AUTODESK INVENTOR PART (.ipt)
format: ipt  version: 2016 (Build 200138000, 138)  size: 852,480 bytes
history: native  units: mm
features: other x69, extrude x8, helix x3, sketch x3, sweep x2, plane x1
ambient origin geometry x8: Origin, YZ Plane, XZ Plane, XY Plane, X Axis, Y Axis, Z Axis, Center Point
bodies: Solid1 (feature_tree)
feature tree (86):
  other  "主线圈路径 (右)"
  other  "剖切工作平面 (右)"
  other  "起始工作平面 (右)"
  other  "结束工作平面 (右)"
  other  "结束切割工作平面 (右)"
  other  "起始切割工作平面 (右)"
  other  "平端切割工作平面 1 (右)"
  other  "平端切割工作平面 2 (右)"
  sweep  "Main Coil Feature(R)"
  other  "起始过渡线圈 1 (右)"
  helix  "Coil  Start Transition 2(R)"  [1 undecoded]
  helix  "Coil  Start Transition 3(R)"  [1 undecoded]
  helix  "Coil  Start Transition 4(R)"  [1 undecoded]
  other  "起始端线圈 (右)"
  extrude  "起始切割特征 (右)"  Depth=10.0mm
  other  "结束过渡线圈 1 (右)"
  other  "结束过渡线圈 2 (右)"
  other  "结束过渡线圈 3 (右)"
  other  "结束过渡线圈 4 (右)"
  other  "结束线圈 (右)"
  extrude  "结束切割特征 (右)"  Depth=10.0mm
  extrude  "平端切割特征 1 (右)"  Depth=10.0mm
  extrude  "Plain Ends Cut  2(R)"  Depth=10.0mm TaperAngle=0.0deg
  other  "主线圈路径 (左)"
  other  "剖切工作平面 (左)"
  other  "起始工作平面 (左)"
  other  "结束工作平面 (左)"
  other  "结束切割工作平面 (左)"
  other  "起始切割工作平面 (左)"
  other  "平端切割工作平面 1 (左)"
  other  "平端切割工作平面 2 (左)"
  sweep  "Main Coil Feature(L)"
  other  "起始过渡线圈 1 (左)"
  other  "起始过渡线圈 2 (左)"
  other  "起始过渡线圈 3 (左)"
  other  "起始过渡线圈 4 (左)"
  other  "起始端线圈 (左)"
  extrude  "起始切割特征 (左)"  Depth=10.0mm TaperAngle=0.0deg
  other  "结束过渡线圈 1 (左)"
  other  "结束过渡线圈 2 (左)"
  other  "结束过渡线圈 3 (左)"
  other  "结束过渡线圈 4 (左)"
  other  "结束线圈 (左)"
  extrude  "结束切割特征 (左)"  Depth=10.0mm
  extrude  "Cut Plain Ends Cut 1(L)"  TaperAngle=0.0deg  [1 undecoded]
  extrude  "Cut Plain Ends Cut 2(L)"  TaperAngle=0.0deg  [1 undecoded]
  other  "iMate 基础工作平面"
  other  "预览中心点"
  other  "预览 X 轴"
  other  "路径截面草图 (右)"
  other  "Srf1"
  other  "线圈截面草图 (右)"
  other  "起始过渡线圈草图 1 (右)"
  sketch  "Sketch  Start Transition 2(R)"  dims[d0=0.075mm d2=1.611283mm d3=10.0mm d4=111.333333mm]
  sketch  "Sketch  Start Transition 3(R)"  dims[d5=0.0mm d6=90.0deg d7=90.0deg d8=0.0mm d9=0.0mm d12=0.893805mm d13=-1.167246mm d14=0.3mm]
  sketch  "Sketch  Start Transition 4(R)"  dims[d15=0.0mm d16=1.283462mm d17=10.0mm d18=2.5mm d19=0.0mm d20=90.0deg d21=90.0deg d22=0.0mm d23=0.0mm d24=0.955642mm d25=10.0mm d26=2.5mm d27=0.0mm d28=90.0deg d29=90.0deg d30=0.0mm d31=0.0mm d32=0.627821mm d33=10.0mm d34=2.5mm d35=0.0mm d36=90.0deg d37=90.0deg d38=0.0mm d39=0.0mm d40=0.3mm d41=10.0mm d42=2.5mm d43=0.0mm d44=90.0deg d45=90.0deg d46=0.0mm d47=0.0mm d48=1.283462mm d49=10.0mm d50=1.875mm d51=0.0mm d52=90.0deg d53=90.0deg d54=0.0mm d55=0.0mm d56=0.955642mm d57=10.0mm d58=1.875mm d59=0.0mm d60=90.0deg d61=90.0deg d62=0.0mm d63=0.0mm d64=0.627821mm d65=10.0mm d66=1.875mm d67=0.0mm d68=90.0deg d69=90.0deg d70=0.0mm d71=0.0mm d72=0.3mm d73=10.0mm d74=1.875mm d75=0.0mm d76=90.0deg d77=90.0deg d78=0.0mm d79=0.0mm d81=10.0mm d82=15.0mm d83=0.0mm d84=90.0deg d85=90.0deg d86=0.0mm d87=0.0mm d88=0.302031mm d89=10.0mm d90=10.0mm d91=0.0mm d92=90.0deg d93=90.0deg d94=0.0mm d95=0.0mm d96=4.7mm d97=0.302031mm d98=0.0mm d99=4.7mm d100=0.302031mm d101=0.0mm d102=0.0mm d103=0.0mm d104=0.0mm d105=0.0mm d106=0.0mm d108=0.0mm d112=0.0mm d113=0.0mm d114=0.0mm d121=0.077532mm d131=0.0mm d132=0.0mm d133=0.0mm d134=0.0mm d135=0.075mm d137=1.611283mm d138=10.0mm d139=111.333333mm d140=0.0mm d141=90.0deg d142=90.0deg d143=0.0mm d144=0.0mm d145=0.893805mm d146=-1.167246mm d147=0.077532mm d148=0.002024mm d149=0.3mm d150=0.0mm d151=0.0mm d152=1.283462mm d153=10.0mm d154=2.5mm d155=0.0mm d156=90.0deg d157=90.0deg d158=0.0mm d159=0.0mm d160=0.955642mm d161=10.0mm d162=2.5mm d163=0.0mm d164=90.0deg d165=90.0deg d166=0.0mm d167=0.0mm d168=0.627821mm d169=10.0mm d170=2.5mm d171=0.0mm d172=90.0deg d173=90.0deg d174=0.0mm d175=0.0mm d176=0.3mm d177=10.0mm d178=2.5mm d179=0.0mm d180=90.0deg d181=90.0deg d182=0.0mm d183=0.0mm d184=10.0mm d185=10.0mm d186=10.0mm d187=10.0mm d188=0.302031mm d189=10.0mm d190=15.0mm d191=0.0mm d192=90.0deg d193=90.0deg d194=0.0mm d195=0.0mm d196=10.0mm d197=4.7mm d198=0.302031mm d199=0.0mm d200=10.0mm d201=1.283462mm d202=10.0mm d203=1.875mm d204=0.0mm d205=90.0deg d206=90.0deg d207=0.0mm d208=0.0mm d209=10.0mm d210=0.955642mm d211=10.0mm d212=1.875mm d213=0.0mm d214=90.0deg d215=90.0deg d216=0.0mm d217=0.0mm d218=0.627821mm d219=10.0mm d220=1.875mm d221=0.0mm d222=90.0deg d223=90.0deg d224=0.0mm d225=0.0mm d226=0.3mm d227=10.0mm d228=1.875mm d229=0.0mm d230=90.0deg d231=90.0deg d232=0.0mm d233=0.0mm d234=10.0mm d235=10.0mm d236=10.0mm d237=0.302031mm d238=10.0mm d239=10.0mm d240=0.0mm d241=90.0deg d242=90.0deg d243=0.0mm d244=0.0mm d245=4.7mm d246=0.302031mm d247=0.0mm d248=10.0mm d249=10.0mm d254=4.7mm d255=10.0mm d256=0.0mm d257=20.0mm d258=-0.002024mm d259=4.7mm d260=10.0mm d261=0.0mm d262=10.0mm d263=4.7mm d264=10.0mm d265=0.0mm d266=10.0mm d267=0.0mm d270=-1.129746mm d271=0.0mm d272=4.7mm d273=10.0mm d274=0.0mm d275=20.0mm d276=-157.079633mm d277=4.4mm d278=4.4mm d279=0.0mm d280=0.0mm]
  other  "结束过渡线圈草图 1 (右)"
  other  "结束过渡线圈草图 2 (右)"
  other  "结束过渡线圈草图 3 (右)"
  other  "结束过渡线圈草图 4 (右)"
  other  "起始端草图 (右)"
  other  "结束线圈草图 (右)"
  other  "结束切割草图 (右)"
  other  "起始切割草图 (右)"
  other  "路径截面草图 (左)"
  other  "Srf2"
  other  "线圈截面草图 (左)"
  other  "起始过渡线圈草图 1 (左)"
  other  "起始过渡线圈草图 2 (左)"
  other  "起始过渡线圈草图 3 (左)"
  other  "起始过渡线圈草图 4 (左)"
  other  "起始端草图 (左)"
  other  "起始切割草图 (左)"
  other  "结束过渡线圈草图 1 (左)"
  other  "结束过渡线圈草图 2 (左)"
  other  "结束过渡线圈草图 3 (左)"
  other  "结束过渡线圈草图 4 (左)"
  other  "结束线圈草图 (左)"
  other  "结束切割草图 (左)"
  other  "平端切割草图 2 (左)"
  other  "平端切割草图 2 (右)"
  other  "平端切割草图 1 (右)"
  other  "平端切割草图 1 (左)"
  plane  "工作平面起始截面"
  other  "基本曲线 (右)"
  other  "基本曲线 (左)"
note: 5 required parameter values undecoded (feature->parameter linkage not recoverable at this tier; creation-order binding heuristic only, values carry confidence <= 0.55)
